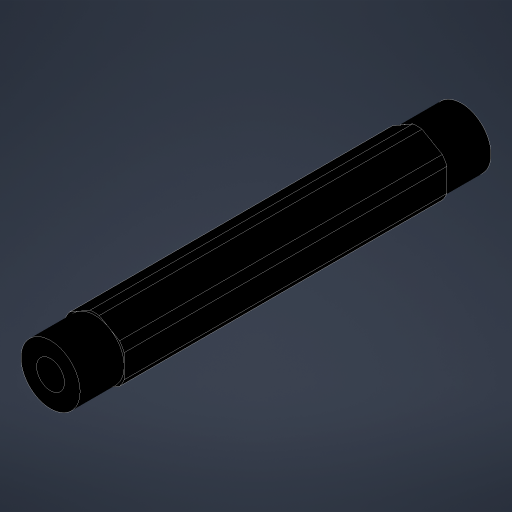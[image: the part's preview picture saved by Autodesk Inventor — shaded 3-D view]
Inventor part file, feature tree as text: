
AUTODESK INVENTOR PART (.ipt)
format: ipt  version: 2023.4 (Build 274418000, 418)  size: 249,344 bytes
history: native  units: in
note: dims shown in document units (in); Inventor stores cm internally (conversion verified against a paired STEP export)
features: extrude x3, projected_geometry x3, hole x1, mirror x1, sketch x1
ambient origin geometry x8: Origin, YZ Plane, XZ Plane, XY Plane, X Axis, Y Axis, Z Axis, Center Point
bodies: Solid1 (feature_tree)
feature tree (9):
  extrude  "Extrusion1"  Depth=0.375in
  hole  "Hole1"  [1 undecoded]
  extrude  "Extrusion3"  Depth=0.28in TaperAngle=0.0deg
  extrude  "Extrusion4"  Depth=0.375in
  mirror  "Mirror2"
  sketch  "Sketch5"  dims[d2=0.0in d9=0.625in d10=0.385in d11=0.25in d12=0.5635in d13=1.0in d14=0.8108in d16=0.7in d17=0.0in d18=0.0in d19=0.28in d20=0.0in d21=0.375in d22=0.5in d23=0.0344in d24=0.5in d25=0.0344in]
  projected_geometry  "Projected Loop2"
  projected_geometry  "Project Cut Edges1"
  projected_geometry  "Project Cut Edges2"
note: 1 required parameter value undecoded (feature->parameter linkage not recoverable at this tier; creation-order binding heuristic only, values carry confidence <= 0.55)
